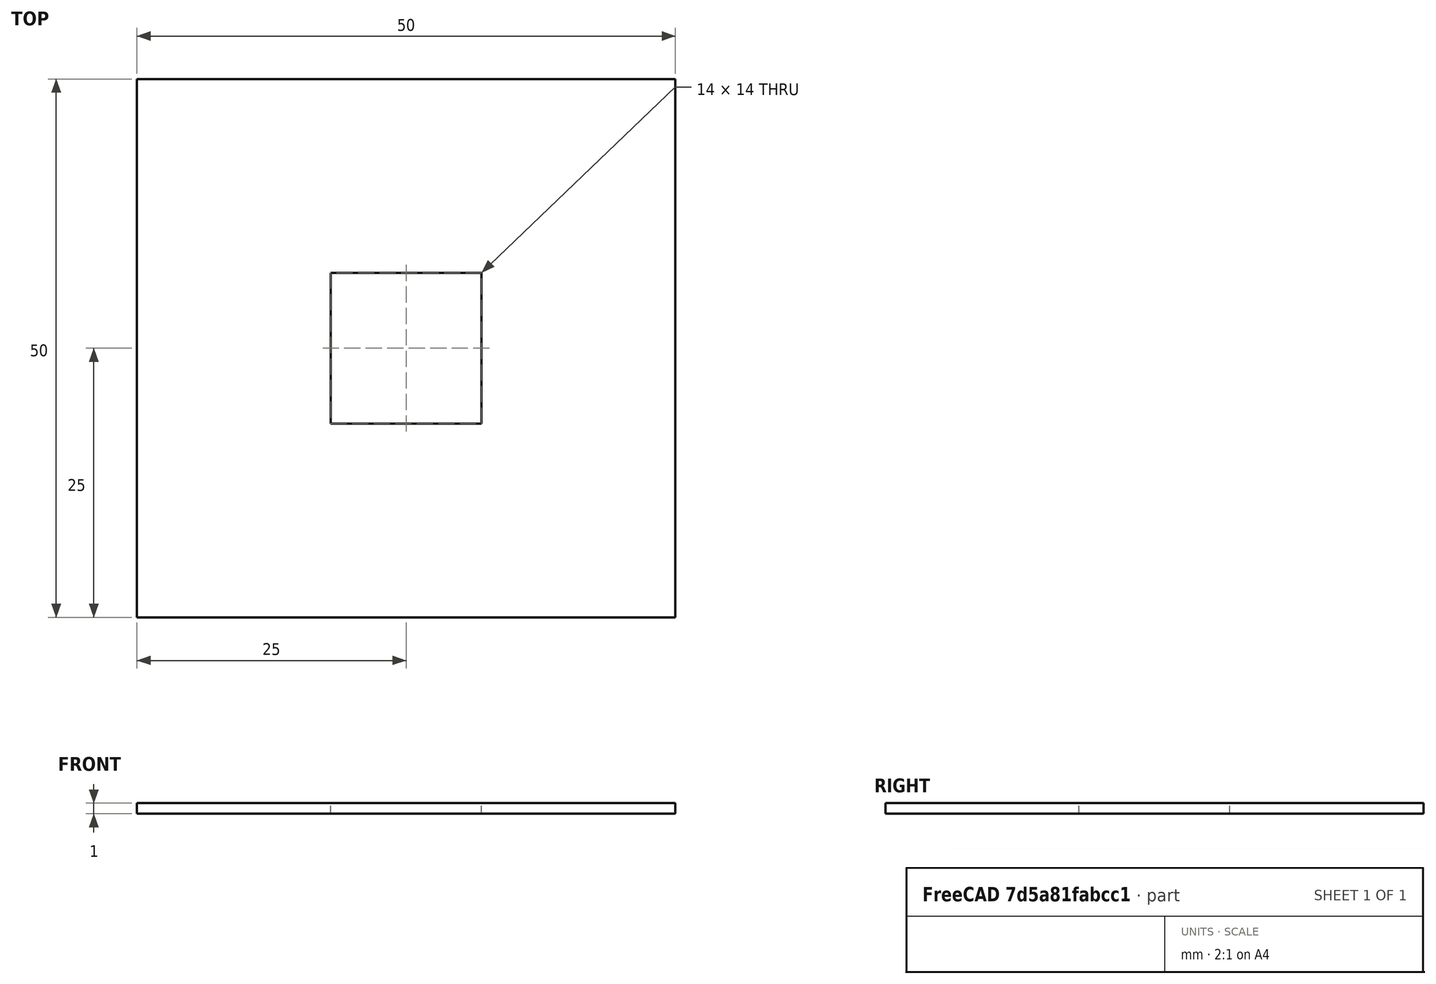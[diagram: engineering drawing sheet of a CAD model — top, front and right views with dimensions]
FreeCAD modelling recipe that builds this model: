
FCSTD DOCUMENT  (FreeCAD 0.18R16161 (Git))
Label: MXterst
License: All rights reserved
LicenseURL: http://en.wikipedia.org/wiki/All_rights_reserved
objects: Sketcher::SketchObject×1, PartDesign::Pad×1, PartDesign::Body×1
note: 4 computed .brp shape members not serialized (recipe doc carries the construction recipe); baked Part::Feature solids carry a one-line shape summary decoded from their .brp

FEATURE [Sketcher::SketchObject] Sketch
  MapMode = 5
  Support = -> [XY_Plane]
  sketch-geometry (8):
    g0: LineSegment StartX=-25 StartY=25 StartZ=0 EndX=25 EndY=25 EndZ=0
    g1: LineSegment StartX=25 StartY=25 StartZ=0 EndX=25 EndY=-25 EndZ=0
    g2: LineSegment StartX=25 StartY=-25 StartZ=0 EndX=-25 EndY=-25 EndZ=0
    g3: LineSegment StartX=-25 StartY=-25 StartZ=0 EndX=-25 EndY=25 EndZ=0
    g4: LineSegment StartX=-7 StartY=7 StartZ=0 EndX=7 EndY=7 EndZ=0
    g5: LineSegment StartX=7 StartY=7 StartZ=0 EndX=7 EndY=-7 EndZ=0
    g6: LineSegment StartX=7 StartY=-7 StartZ=0 EndX=-7 EndY=-7 EndZ=0
    g7: LineSegment StartX=-7 StartY=-7 StartZ=0 EndX=-7 EndY=7 EndZ=0
  constraints (16):
    c: Coincident(g0,g1)
    c: Coincident(g1,g2)
    c: Coincident(g2,g3)
    c: Coincident(g3,g0)
    c: Horizontal(g0)
    c: Horizontal(g2)
    c: Vertical(g1)
    c: Vertical(g3)
    c: Coincident(g4,g5)
    c: Coincident(g5,g6)
    c: Coincident(g6,g7)
    c: Coincident(g7,g4)
    c: Horizontal(g4)
    c: Horizontal(g6)
    c: Vertical(g5)
    c: Vertical(g7)
FEATURE [PartDesign::Pad] Pad
  Length = 1
  Length2 = 100
  Profile = -> Sketch
  Type = 0
FEATURE [PartDesign::Body] Body
  Group = -> [Sketch,Pad]
  Origin = -> Origin
  Tip = -> Pad
